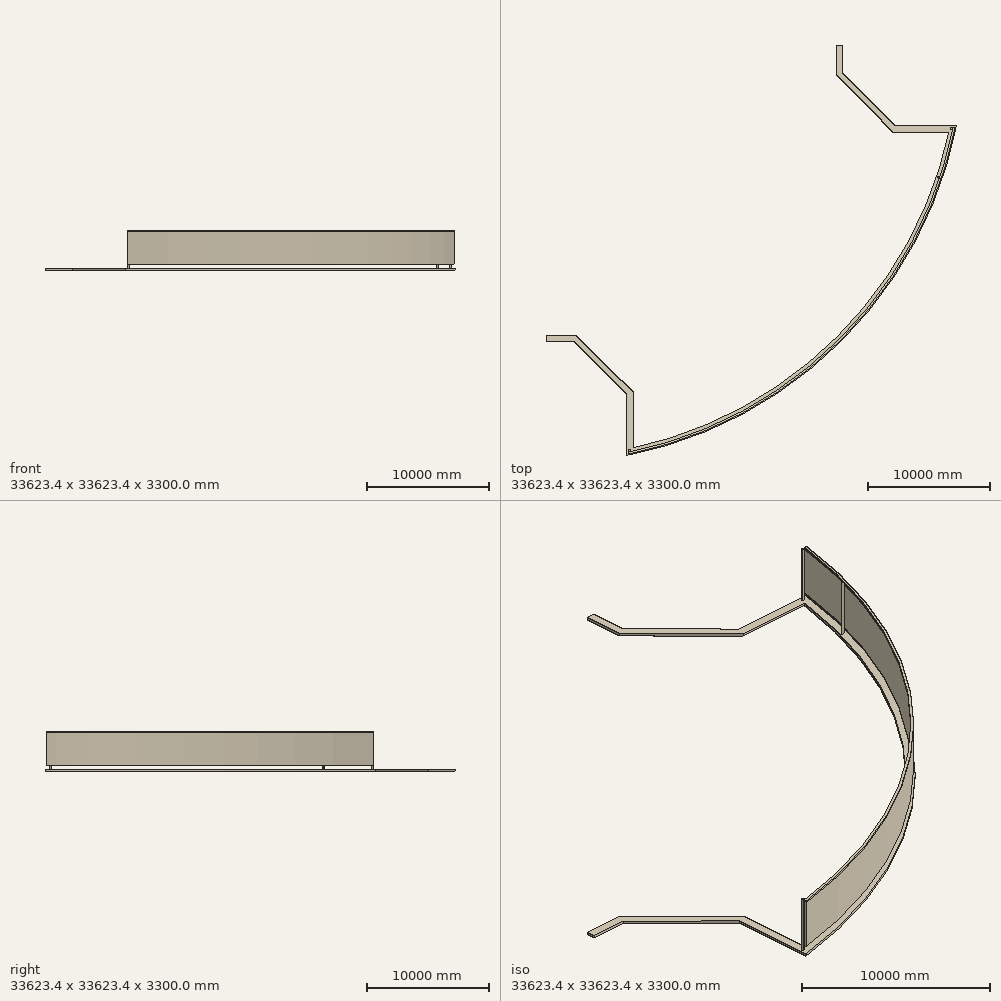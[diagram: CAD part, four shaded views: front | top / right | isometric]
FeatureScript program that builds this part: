
annotation { "Feature Type Name" : "Feature", "Feature Type Description" : "" }
export const myFeature = defineFeature(function(context is Context, id is Id, definition is map)
    precondition{}
    {
        {
            var Q0;
            Q0=qCreatedBy(makeId("Top.planeOp"),FACE);
            var sketch = newSketch(context, id + "F0", { "sketchPlane" : qUnion([Q0])});
            skArc(sketch, "E0", {"start": v(0, -34265) * mm, "mid": v(24229.01, -24229.01) * mm, "end": v(34265, 0) * mm, "construction": true});
            skArc(sketch, "E1", {"start": v(0, -33765) * mm, "mid": v(23875.46, -23875.46) * mm, "end": v(33765, 0) * mm, "construction": true});
            skArc(sketch, "E2", {"start": v(0, -34015) * mm, "mid": v(24052.24, -24052.24) * mm, "end": v(34015, 0) * mm, "construction": true});
            skLineSegment(sketch, "E3", {"start": v(0, 0) * mm, "end": v(34265, 0) * mm, "construction": true});
            skLineSegment(sketch, "E4", {"start": v(34265, 0) * mm, "end": v(0, 0) * mm, "construction": true});
            skLineSegment(sketch, "E5", {"start": v(0, -34265) * mm, "end": v(0, 0) * mm, "construction": true});
            skSolve(sketch);
        }
        {
            var Q0;
            Q0=qCreatedBy(makeId("Top.planeOp"),FACE);
            var sketch = newSketch(context, id + "F1", { "sketchPlane" : qUnion([Q0])});
            skArc(sketch, "E6.0", {"start": v(0, -33765) * mm, "mid": v(23875.46, -23875.46) * mm, "end": v(33765, 0) * mm, "construction": true});
            skArc(sketch, "E7.0", {"start": v(6600, -33368.55) * mm, "mid": v(26282.3, -21593.07) * mm, "end": v(34015, 0) * mm, "construction": true});
            skArc(sketch, "E8.0", {"start": v(0, -34265) * mm, "mid": v(24229.01, -24229.01) * mm, "end": v(34265, 0) * mm, "construction": true});
            skArc(sketch, "E9", {"start": v(6600, -33623.36) * mm, "mid": v(24229.01, -24229.01) * mm, "end": v(33623.36, -6600) * mm});
            skArc(sketch, "E10", {"start": v(7100, -33010.08) * mm, "mid": v(23875.46, -23875.46) * mm, "end": v(33010.08, -7100) * mm});
            skLineSegment(sketch, "E11", {"start": v(23755.3, 0) * mm, "end": v(24255.3, 0) * mm});
            skLineSegment(sketch, "E12", {"start": v(0, -23755.3) * mm, "end": v(0, -24255.3) * mm});
            skLineSegment(sketch, "E13", {"start": v(28623.36, -6600) * mm, "end": v(33623.36, -6600) * mm});
            skLineSegment(sketch, "E14", {"start": v(28623.36, -6600) * mm, "end": v(24255.3, -2200) * mm});
            skLineSegment(sketch, "E15", {"start": v(24255.3, -2200) * mm, "end": v(24255.3, 0) * mm});
            skLineSegment(sketch, "E16", {"start": v(6600, -28623.36) * mm, "end": v(6600, -33623.36) * mm});
            skLineSegment(sketch, "E17", {"start": v(6600, -28623.36) * mm, "end": v(2200, -24255.3) * mm});
            skLineSegment(sketch, "E18", {"start": v(2200, -24255.3) * mm, "end": v(0, -24255.3) * mm});
            skPoint(sketch, "E19.orphan", {"position": v(0, -34015) * mm});
            skLineSegment(sketch, "E20.trimOffspring", {"start": v(0, -33765) * mm, "end": v(0, -34265) * mm});
            skLineSegment(sketch, "E21", {"start": v(33010.08, -7100) * mm, "end": v(28415.18, -7100) * mm});
            skLineSegment(sketch, "E22", {"start": v(28415.18, -7100) * mm, "end": v(23755.3, -2406.04) * mm});
            skLineSegment(sketch, "E23", {"start": v(23755.3, 0) * mm, "end": v(23755.3, -2406.04) * mm});
            skLineSegment(sketch, "E24", {"start": v(7100, -28415.18) * mm, "end": v(7100, -33010.08) * mm});
            skLineSegment(sketch, "E25", {"start": v(7100, -28415.18) * mm, "end": v(2406.04, -23755.3) * mm});
            skLineSegment(sketch, "E26", {"start": v(0, -23755.3) * mm, "end": v(2406.04, -23755.3) * mm});
            skSolve(sketch);
        }
        {
            var Q0;
            Q0 = qSketchRegion(id + "F1", true);
            extrude(context, id + "F2", {"entities" : qUnion([Q0]), "depth" : 150 * mm});
        }
        {
            var Q0;
            Q0=qCreatedBy(makeId("Top.planeOp"),FACE);
            var sketch = newSketch(context, id + "F3", { "sketchPlane" : qUnion([Q0])});
            skLineSegment(sketch, "E27.bottom", {"start": v(33140, -6850) * mm, "end": v(33290, -6850) * mm});
            skLineSegment(sketch, "E27.top", {"start": v(33140, -6750) * mm, "end": v(33290, -6750) * mm});
            skLineSegment(sketch, "E27.left", {"start": v(33140, -6750) * mm, "end": v(33140, -6850) * mm});
            skLineSegment(sketch, "E27.right", {"start": v(33290, -6750) * mm, "end": v(33290, -6850) * mm});
            skLineSegment(sketch, "E28", {"start": v(33215, -6483.1) * mm, "end": v(33215, -7058.76) * mm, "construction": true});
            skLineSegment(sketch, "E29.bottom", {"start": v(6750, -33140) * mm, "end": v(6850, -33140) * mm});
            skLineSegment(sketch, "E29.top", {"start": v(6750, -33290) * mm, "end": v(6850, -33290) * mm});
            skLineSegment(sketch, "E29.left", {"start": v(6750, -33140) * mm, "end": v(6750, -33290) * mm});
            skLineSegment(sketch, "E29.right", {"start": v(6850, -33140) * mm, "end": v(6850, -33290) * mm});
            skSolve(sketch);
        }
        {
            var Q0;
            Q0 = qSketchRegion(id + "F3", true);
            extrude(context, id + "F4", {"entities" : qUnion([Q0]), "operationType" : NewBodyOperationType.ADD, "depth" : 3300 * mm});
        }
        {
            var Q0;
            Q0=qCreatedBy(makeId("Right.planeOp"),FACE);
            var sketch = newSketch(context, id + "F5", { "sketchPlane" : qUnion([Q0])});
            skPoint(sketch, "E30.0", {"position": v(0, 0) * mm});
            skLineSegment(sketch, "E31", {"start": v(0, 0) * mm, "end": v(0, 7479.54) * mm, "construction": true});
            skSolve(sketch);
        }
        {
            var Q0;
            Q0=qCreatedBy(makeId("Top.planeOp"),FACE);
            var sketch = newSketch(context, id + "F6", { "sketchPlane" : qUnion([Q0])});
            skLineSegment(sketch, "E32", {"start": v(0, 0) * mm, "end": v(37045.14, -12467.07) * mm, "construction": true});
            skArc(sketch, "E33.0", {"start": v(0, -34015) * mm, "mid": v(24052.24, -24052.24) * mm, "end": v(34015, 0) * mm, "construction": true});
            skArc(sketch, "E34.0", {"start": v(0, -34265) * mm, "mid": v(24229.01, -24229.01) * mm, "end": v(34265, 0) * mm, "construction": true});
            skArc(sketch, "E35.0", {"start": v(0, -33765) * mm, "mid": v(23875.46, -23875.46) * mm, "end": v(33765, 0) * mm, "construction": true});
            skLineSegment(sketch, "E36", {"start": v(32096.18, -10801.56) * mm, "end": v(32112.13, -10754.17) * mm});
            skLineSegment(sketch, "E37", {"start": v(32112.13, -10754.17) * mm, "end": v(32254.3, -10802.01) * mm});
            skLineSegment(sketch, "E38", {"start": v(32222.4, -10896.79) * mm, "end": v(32080.23, -10848.95) * mm});
            skLineSegment(sketch, "E39", {"start": v(32080.23, -10848.95) * mm, "end": v(32096.18, -10801.56) * mm});
            skLineSegment(sketch, "E40", {"start": v(32254.3, -10802.01) * mm, "end": v(32238.34, -10849.4) * mm});
            skLineSegment(sketch, "E41", {"start": v(32238.34, -10849.4) * mm, "end": v(32222.4, -10896.79) * mm});
            skSolve(sketch);
        }
        {
            var Q0;
            Q0 = qSketchRegion(id + "F6", true);
            extrude(context, id + "F7", {"entities" : qUnion([Q0]), "operationType" : NewBodyOperationType.ADD, "depth" : 3300 * mm});
        }
        {
            var Q0;
            Q0=qCreatedBy(makeId("Front.planeOp"),FACE);
            var sketch = newSketch(context, id + "F8", { "sketchPlane" : qUnion([Q0])});
            skLineSegment(sketch, "E42", {"start": v(34035, 3300) * mm, "end": v(34185, 3300) * mm});
            skLineSegment(sketch, "E43", {"start": v(34185, 3300) * mm, "end": v(34185, 3200) * mm});
            skLineSegment(sketch, "E44", {"start": v(34185, 3200) * mm, "end": v(34179, 3200) * mm});
            skLineSegment(sketch, "E45", {"start": v(34179, 3200) * mm, "end": v(34179, 3294) * mm});
            skLineSegment(sketch, "E46", {"start": v(34179, 3294) * mm, "end": v(34041, 3294) * mm});
            skLineSegment(sketch, "E47", {"start": v(34041, 3294) * mm, "end": v(34041, 3200) * mm});
            skPoint(sketch, "E48.0.end.orphan", {"position": v(33290, 150) * mm});
            skLineSegment(sketch, "E49", {"start": v(34035, 3300) * mm, "end": v(34035, 3200) * mm});
            skLineSegment(sketch, "E50", {"start": v(34035, 3200) * mm, "end": v(34041, 3200) * mm});
            skSolve(sketch);
        }
        {
            var Q0;
            Q0 = qSketchRegion(id + "F8", true);
            var Q1;
            Q1=sQuery(id+"F5.wireOp",EDGE,"E31");
            revolve(context, id + "F9", {"entities" : qUnion([Q0]), "axis" : qUnion([Q1]), "revolveType" : RevolveType.ONE_DIRECTION, "oppositeDirection" : true, "angle" : 90 * degree});
        }
        {
            var Q0;
            Q0=qCreatedBy(makeId("Front.planeOp"),FACE);
            var sketch = newSketch(context, id + "F10", { "sketchPlane" : qUnion([Q0])});
            skLineSegment(sketch, "E51.0", {"start": v(34041, 3294) * mm, "end": v(34041, 3200) * mm, "construction": true});
            skLineSegment(sketch, "E52.0", {"start": v(34179, 3294) * mm, "end": v(34041, 3294) * mm, "construction": true});
            skLineSegment(sketch, "E53.0", {"start": v(34179, 3200) * mm, "end": v(34179, 3294) * mm, "construction": true});
            skLineSegment(sketch, "E54.bottom", {"start": v(34043.5, 3289) * mm, "end": v(34176.5, 3289) * mm});
            skLineSegment(sketch, "E54.top", {"start": v(34043.5, 489) * mm, "end": v(34176.5, 489) * mm});
            skLineSegment(sketch, "E54.left", {"start": v(34043.5, 3289) * mm, "end": v(34043.5, 489) * mm});
            skLineSegment(sketch, "E54.right", {"start": v(34176.5, 3289) * mm, "end": v(34176.5, 489) * mm});
            skSolve(sketch);
        }
        {
            var Q0;
            Q0 = qSketchRegion(id + "F10", true);
            var Q1;
            Q1=sQuery(id+"F5.wireOp",EDGE,"E31");
            revolve(context, id + "F11", {"entities" : qUnion([Q0]), "axis" : qUnion([Q1]), "revolveType" : RevolveType.ONE_DIRECTION, "oppositeDirection" : true, "angle" : 90 * degree});
        }
        {
            var Q0;
            Q0=qCreatedBy(makeId("Front.planeOp"),FACE);
            var sketch = newSketch(context, id + "F12", { "sketchPlane" : qUnion([Q0])});
            skLineSegment(sketch, "E55.0", {"start": v(0, 0) * mm, "end": v(0, 7479.54) * mm, "construction": true});
            skLineSegment(sketch, "E56.0", {"start": v(6750, 3300) * mm, "end": v(6750, 150) * mm, "construction": true});
            skLineSegment(sketch, "E57.bottom", {"start": v(0, 3980.53) * mm, "end": v(6750, 3980.53) * mm});
            skLineSegment(sketch, "E57.top", {"start": v(0, 286.05) * mm, "end": v(6750, 286.05) * mm});
            skLineSegment(sketch, "E57.left", {"start": v(0, 3980.53) * mm, "end": v(0, 286.05) * mm});
            skLineSegment(sketch, "E57.right", {"start": v(6750, 3980.53) * mm, "end": v(6750, 286.05) * mm});
            skSolve(sketch);
        }
        {
            var Q0;
            Q0=makeQuery(id+"F12.imprint","IMPRINT",FACE,{"disambiguationData":[TD([[makeQuery(id+"F12.imprint","IMPRINT",EDGE,{"derivedFrom":sQuery(id+"F12.wireOp",EDGE,"E57.bottom")}),-1.0]])]});
            extrude(context, id + "F13", {"entities" : qUnion([Q0]), "operationType" : NewBodyOperationType.REMOVE, "endBound" : BoundingType.THROUGH_ALL, "depth" : 25 * mm});
        }
        {
            var Q0;
            Q0=qCreatedBy(makeId("Right.planeOp"),FACE);
            var sketch = newSketch(context, id + "F14", { "sketchPlane" : qUnion([Q0])});
            skLineSegment(sketch, "E58.0", {"start": v(0, 0) * mm, "end": v(0, 7479.54) * mm, "construction": true});
            skLineSegment(sketch, "E59.0", {"start": v(-6750, 3300) * mm, "end": v(-6750, 150) * mm, "construction": true});
            skLineSegment(sketch, "E60.bottom", {"start": v(0, 4365.97) * mm, "end": v(-6750, 4365.97) * mm});
            skLineSegment(sketch, "E60.top", {"start": v(0, 325.42) * mm, "end": v(-6750, 325.42) * mm});
            skLineSegment(sketch, "E60.left", {"start": v(0, 4365.97) * mm, "end": v(0, 325.42) * mm});
            skLineSegment(sketch, "E60.right", {"start": v(-6750, 4365.97) * mm, "end": v(-6750, 325.42) * mm});
            skSolve(sketch);
        }
        {
            var Q0;
            Q0=makeQuery(id+"F14.imprint","IMPRINT",FACE,{"disambiguationData":[TD([[makeQuery(id+"F14.imprint","IMPRINT",EDGE,{"derivedFrom":sQuery(id+"F14.wireOp",EDGE,"E60.bottom")}),1.0]])]});
            extrude(context, id + "F15", {"entities" : qUnion([Q0]), "operationType" : NewBodyOperationType.REMOVE, "endBound" : BoundingType.THROUGH_ALL, "depth" : 25 * mm});
        }
    });
